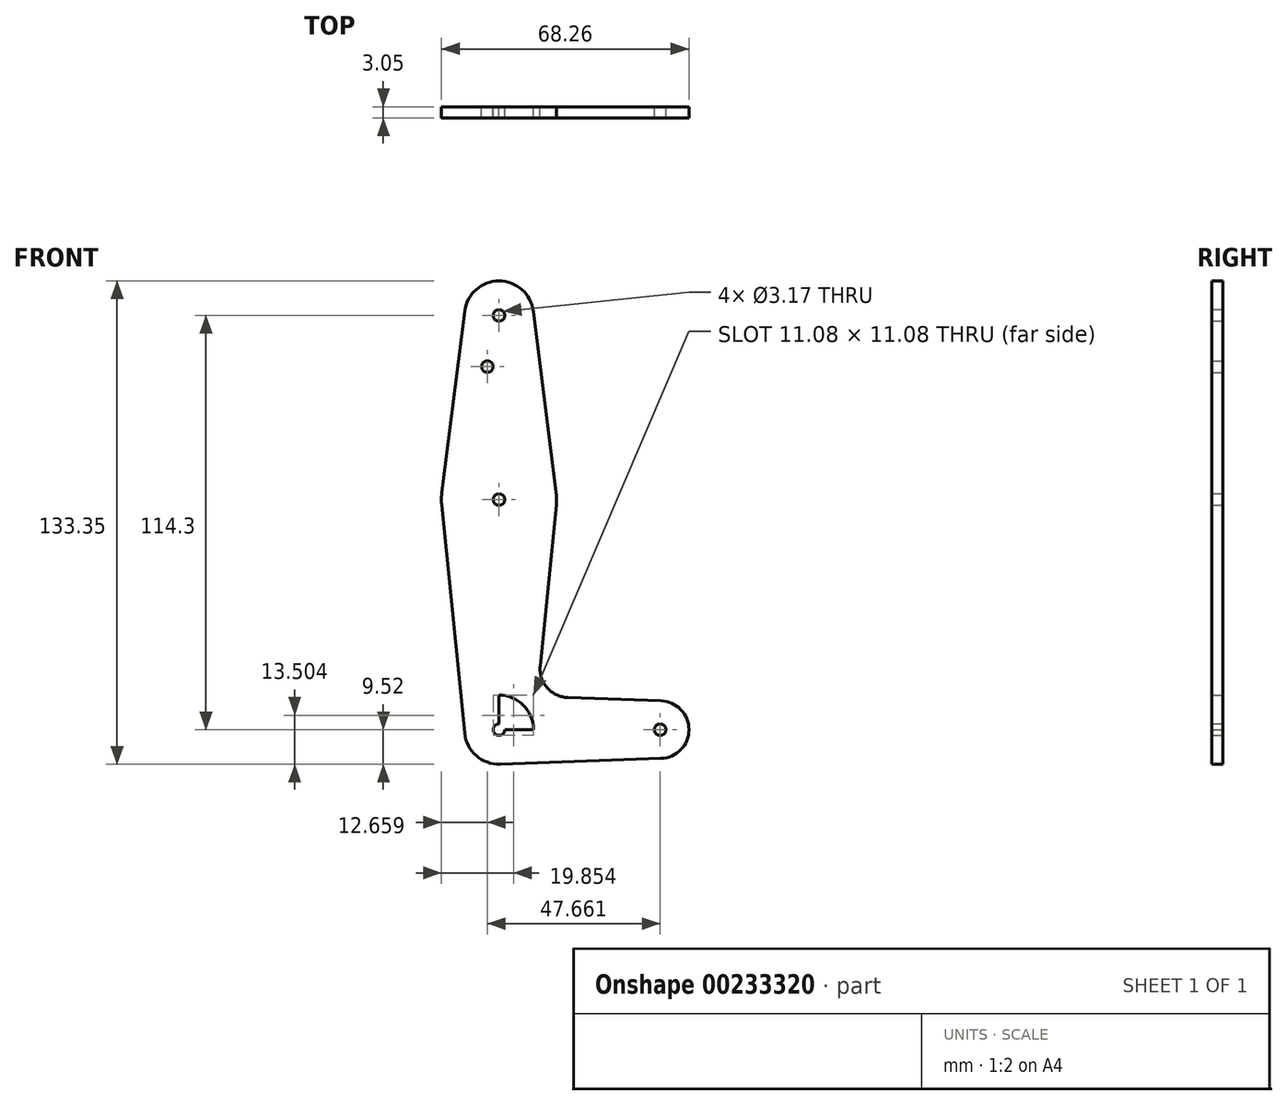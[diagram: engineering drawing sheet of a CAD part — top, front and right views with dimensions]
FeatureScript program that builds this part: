
annotation { "Feature Type Name" : "Feature", "Feature Type Description" : "" }
export const myFeature = defineFeature(function(context is Context, id is Id, definition is map)
    precondition{}
    {
        {
            var Q0;
            Q0=qCreatedBy(makeId("Front.planeOp"),FACE);
            var sketch = newSketch(context, id + "F0", { "sketchPlane" : qUnion([Q0])});
            skCircle(sketch, "E0", {"center": v(0, 0) * mm, "radius": 9.53 * mm});
            skCircle(sketch, "E1", {"center": v(0, 63.5) * mm, "radius": 15.88 * mm});
            skLineSegment(sketch, "E2", {"start": v(0, 0) * mm, "end": v(0, 63.5) * mm});
            skLineSegment(sketch, "E3", {"start": v(0, 63.5) * mm, "end": v(0, 114.3) * mm});
            skCircle(sketch, "E4", {"center": v(0, 114.3) * mm, "radius": 9.53 * mm});
            skLineSegment(sketch, "E5", {"start": v(0, 0) * mm, "end": v(44.45, 0) * mm});
            skCircle(sketch, "E6", {"center": v(44.45, 0) * mm, "radius": 7.94 * mm});
            skLineSegment(sketch, "E7", {"start": v(-15.8, 61.91) * mm, "end": v(-9.48, -0.95) * mm});
            skLineSegment(sketch, "E8", {"start": v(15.8, 61.91) * mm, "end": v(11.34, 17.6) * mm});
            skLineSegment(sketch, "E9", {"start": v(-15.75, 65.48) * mm, "end": v(-9.45, 115.5) * mm});
            skLineSegment(sketch, "E10", {"start": v(15.75, 65.48) * mm, "end": v(9.45, 115.5) * mm});
            skLineSegment(sketch, "E11", {"start": v(18.97, 8.85) * mm, "end": v(44.73, 7.93) * mm});
            skLineSegment(sketch, "E12", {"start": v(0.34, -9.52) * mm, "end": v(44.73, -7.93) * mm});
            skArc(sketch, "E13.filletArc", {"start": v(11.34, 17.6) * mm, "mid": v(13.26, 11.57) * mm, "end": v(18.97, 8.85) * mm});
            skCircle(sketch, "E14", {"center": v(0, 114.3) * mm, "radius": 1.59 * mm});
            skCircle(sketch, "E15", {"center": v(0, 0) * mm, "radius": 1.59 * mm});
            skCircle(sketch, "E16", {"center": v(0, 63.5) * mm, "radius": 1.59 * mm});
            skCircle(sketch, "E17", {"center": v(44.45, 0) * mm, "radius": 1.59 * mm});
            skCircle(sketch, "E18", {"center": v(-3.21, 100.17) * mm, "radius": 1.59 * mm});
            skSolve(sketch);
        }
        {
            var Q0;
            Q0 = qSketchRegion(id + "F0", true);
            extrude(context, id + "F1", {"entities" : qUnion([Q0]), "depth" : 3.05 * mm});
        }
    });
